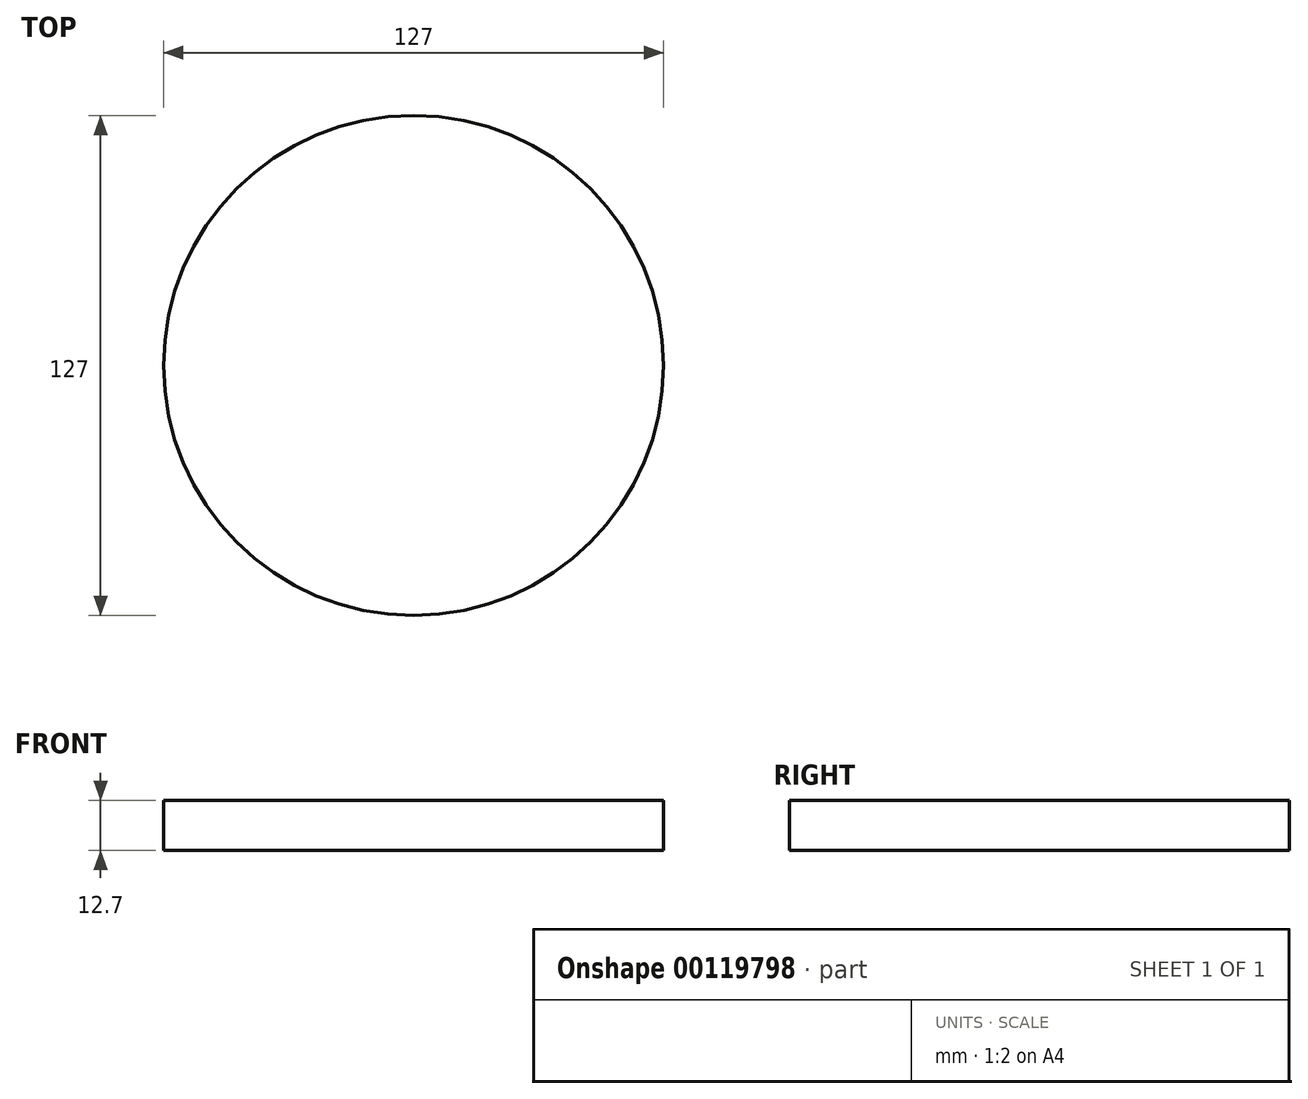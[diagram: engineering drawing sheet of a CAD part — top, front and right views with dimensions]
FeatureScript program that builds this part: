
annotation { "Feature Type Name" : "Feature", "Feature Type Description" : "" }
export const myFeature = defineFeature(function(context is Context, id is Id, definition is map)
    precondition{}
    {
        {
            var Q0;
            Q0=qCreatedBy(makeId("Top.planeOp"),FACE);
            var sketch = newSketch(context, id + "F0", { "sketchPlane" : qUnion([Q0])});
            skCircle(sketch, "E0", {"center": v(-56.11, -46.93) * mm, "radius": 63.5 * mm});
            skSolve(sketch);
        }
        {
            var Q0;
            Q0 = qSketchRegion(id + "F0", true);
            extrude(context, id + "F1", {"entities" : qUnion([Q0]), "depth" : 12.7 * mm});
        }
    });
